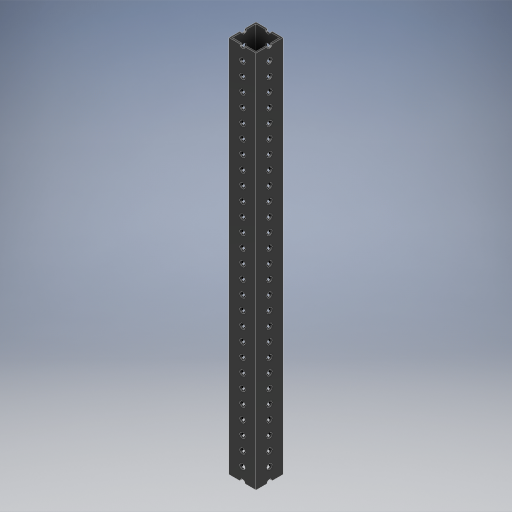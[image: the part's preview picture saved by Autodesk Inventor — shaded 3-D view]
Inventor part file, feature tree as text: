
AUTODESK INVENTOR PART (.ipt)
format: ipt  version: 2024.2 (Build 282272000, 272)  size: 501,760 bytes
history: native  units: in
note: dims shown in document units (in); Inventor stores cm internally (conversion verified against a paired STEP export)
features: projected_geometry x8, other x4, extrude x1, sketch x1
ambient origin geometry x8: Origin, YZ Plane, XZ Plane, XY Plane, X Axis, Y Axis, Z Axis, Center Point
bodies: Body1 (feature_tree)
feature tree (14):
  other  "2024-210-003-Front-Angle"
  other  "2024-210-000-Fixed-Shootaur.ipt"
  extrude  "Extrusion1"  Depth=0.3937in TaperAngle=0.0deg
  other  "2024-210-003-Front-Angle::2024-210-000-Fixed-Shootaur.ipt"
  other  "TaggingFeature1"
  sketch  "Sketch1"  dims[d0=0.3937in d1=1.5in d2=0.0in]
  projected_geometry  "Projected Loop1"
  projected_geometry  "Projected Loop2"
  projected_geometry  "Projected Loop3"
  projected_geometry  "Projected Loop4"
  projected_geometry  "Projected Loop5"
  projected_geometry  "Projected Loop6"
  projected_geometry  "Projected Loop7"
  projected_geometry  "Projected Loop8"
